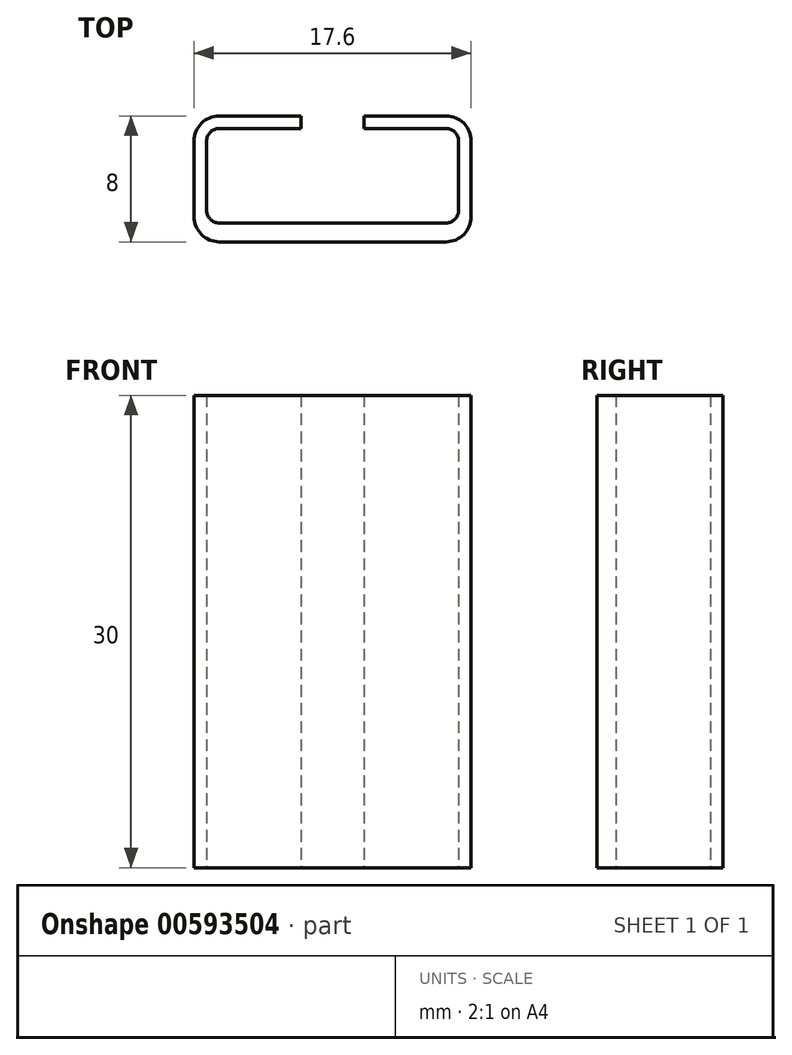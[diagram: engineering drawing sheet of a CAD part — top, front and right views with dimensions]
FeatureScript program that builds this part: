
annotation { "Feature Type Name" : "Feature", "Feature Type Description" : "" }
export const myFeature = defineFeature(function(context is Context, id is Id, definition is map)
    precondition{}
    {
        {
            var Q0;
            Q0=qCreatedBy(makeId("Top.planeOp"),FACE);
            var sketch = newSketch(context, id + "F0", { "sketchPlane" : qUnion([Q0])});
            skLineSegment(sketch, "E0", {"start": v(-17.6, 1.6) * mm, "end": v(-17.6, 6.4) * mm});
            skLineSegment(sketch, "E1", {"start": v(-16, 8) * mm, "end": v(-10.8, 8) * mm});
            skLineSegment(sketch, "E2", {"start": v(-10.8, 8) * mm, "end": v(-10.8, 7.2) * mm});
            skLineSegment(sketch, "E3", {"start": v(-10.8, 7.2) * mm, "end": v(-16, 7.2) * mm});
            skLineSegment(sketch, "E4", {"start": v(-16.8, 6.4) * mm, "end": v(-16.8, 2) * mm});
            skLineSegment(sketch, "E5", {"start": v(-16, 1.2) * mm, "end": v(-1.6, 1.2) * mm});
            skLineSegment(sketch, "E6", {"start": v(-0.8, 2) * mm, "end": v(-0.8, 6.4) * mm});
            skLineSegment(sketch, "E7", {"start": v(-1.6, 7.2) * mm, "end": v(-6.8, 7.2) * mm});
            skLineSegment(sketch, "E8", {"start": v(-6.8, 7.2) * mm, "end": v(-6.8, 8) * mm});
            skLineSegment(sketch, "E9", {"start": v(-6.8, 8) * mm, "end": v(-1.6, 8) * mm});
            skLineSegment(sketch, "E10", {"start": v(0, 6.4) * mm, "end": v(0, 1.6) * mm});
            skLineSegment(sketch, "E11", {"start": v(-1.6, 0) * mm, "end": v(-16, 0) * mm});
            skPoint(sketch, "E12.visualSharp", {"position": v(0, 0) * mm});
            skArc(sketch, "E12.filletArc", {"start": v(-1.6, 0) * mm, "mid": v(-0.47, 0.47) * mm, "end": v(0, 1.6) * mm});
            skPoint(sketch, "E13.visualSharp", {"position": v(-17.6, 0) * mm});
            skArc(sketch, "E13.filletArc", {"start": v(-17.6, 1.6) * mm, "mid": v(-17.13, 0.47) * mm, "end": v(-16, 0) * mm});
            skPoint(sketch, "E14.visualSharp", {"position": v(-17.6, 8) * mm});
            skArc(sketch, "E14.filletArc", {"start": v(-16, 8) * mm, "mid": v(-17.13, 7.53) * mm, "end": v(-17.6, 6.4) * mm});
            skPoint(sketch, "E15.visualSharp", {"position": v(0, 8) * mm});
            skArc(sketch, "E15.filletArc", {"start": v(0, 6.4) * mm, "mid": v(-0.47, 7.53) * mm, "end": v(-1.6, 8) * mm});
            skPoint(sketch, "E16.visualSharp", {"position": v(-16.8, 7.2) * mm});
            skArc(sketch, "E16.filletArc", {"start": v(-16, 7.2) * mm, "mid": v(-16.57, 6.97) * mm, "end": v(-16.8, 6.4) * mm});
            skPoint(sketch, "E17.visualSharp", {"position": v(-16.8, 1.2) * mm});
            skArc(sketch, "E17.filletArc", {"start": v(-16.8, 2) * mm, "mid": v(-16.57, 1.43) * mm, "end": v(-16, 1.2) * mm});
            skPoint(sketch, "E18.visualSharp", {"position": v(-0.8, 1.2) * mm});
            skArc(sketch, "E18.filletArc", {"start": v(-1.6, 1.2) * mm, "mid": v(-1.03, 1.43) * mm, "end": v(-0.8, 2) * mm});
            skPoint(sketch, "E19.visualSharp", {"position": v(-0.8, 7.2) * mm});
            skArc(sketch, "E19.filletArc", {"start": v(-0.8, 6.4) * mm, "mid": v(-1.03, 6.97) * mm, "end": v(-1.6, 7.2) * mm});
            skSolve(sketch);
        }
        {
            var Q0;
            Q0=makeQuery(id+"F0.imprint","IMPRINT",FACE,{"disambiguationData":[TD([[makeQuery(id+"F0.imprint","IMPRINT",EDGE,{"derivedFrom":sQuery(id+"F0.wireOp",EDGE,"E0")}),-1.0]])]});
            extrude(context, id + "F1", {"entities" : qUnion([Q0]), "depth" : 30 * mm, "offsetDistance" : 25 * mm});
        }
    });
